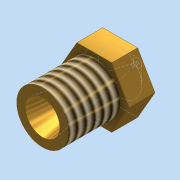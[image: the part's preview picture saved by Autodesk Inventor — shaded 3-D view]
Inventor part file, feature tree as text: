
AUTODESK INVENTOR PART (.ipt)
format: ipt  version: 2016 (Build 200138000, 138)  size: 144,384 bytes
history: native  units: mm
features: sketch x4, extrude x3, chamfer x1, hole x1, thread x1
ambient origin geometry x8: Origin, YZ Plane, XZ Plane, XY Plane, X Axis, Y Axis, Z Axis, Center Point
bodies: Solid1 (feature_tree)
feature tree (10):
  extrude  "Extrusion1"  Depth=6.0mm TaperAngle=0.0deg
  extrude  "Extrusion2"  Depth=3.0mm TaperAngle=0.0deg
  extrude  "Extrusion3"  Depth=2.0mm TaperAngle=0.0deg
  chamfer  "Chamfer1"  Distance=2.0mm Angle=45.0deg
  hole  "Hole1"  [1 undecoded]
  thread  "Thread1"  [1 undecoded]
  sketch  "Sketch1"  dims[d0=6.0mm d1=6.0mm d2=0.0mm]
  sketch  "Sketch2"  dims[d3=7.0mm d4=3.0mm d5=0.0mm]
  sketch  "Sketch3"  dims[d6=5.0mm d7=2.0mm d8=0.0mm d9=2.0mm d10=2.0mm d11=45.0deg]
  sketch  "Sketch4"  dims[d12=0.3mm d13=6.0mm d14=4.0mm d15=2.0mm d16=3.490659mm d17=8.0mm d18=20.594885mm d19=10.0mm d20=0.0mm]
note: 2 required parameter values undecoded (feature->parameter linkage not recoverable at this tier; creation-order binding heuristic only, values carry confidence <= 0.55)
